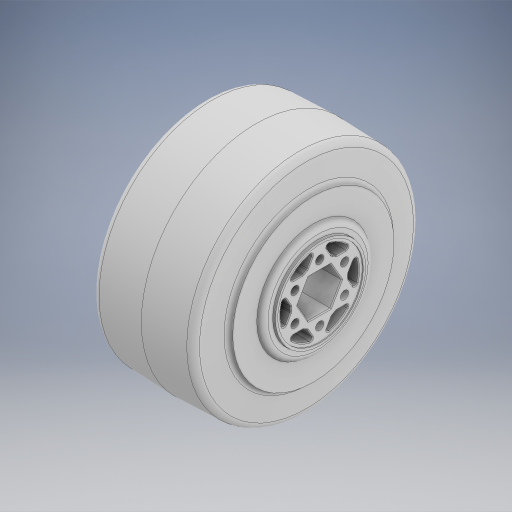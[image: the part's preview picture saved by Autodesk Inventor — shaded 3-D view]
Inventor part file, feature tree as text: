
AUTODESK INVENTOR PART (.ipt)
format: ipt  version: 2024.2 (Build 282272000, 272)  size: 1,282,560 bytes
history: native  units: in
note: dims shown in document units (in); Inventor stores cm internally (conversion verified against a paired STEP export)
features: revolve x1
ambient origin geometry x8: Origin, YZ Plane, XZ Plane, XY Plane, X Axis, Y Axis, Z Axis, Center Point
bodies: Solid1 (feature_tree)
feature tree (1):
  revolve  "Revolve1"  [1 undecoded]
note: 1 required parameter value undecoded (feature->parameter linkage not recoverable at this tier; creation-order binding heuristic only, values carry confidence <= 0.55)
